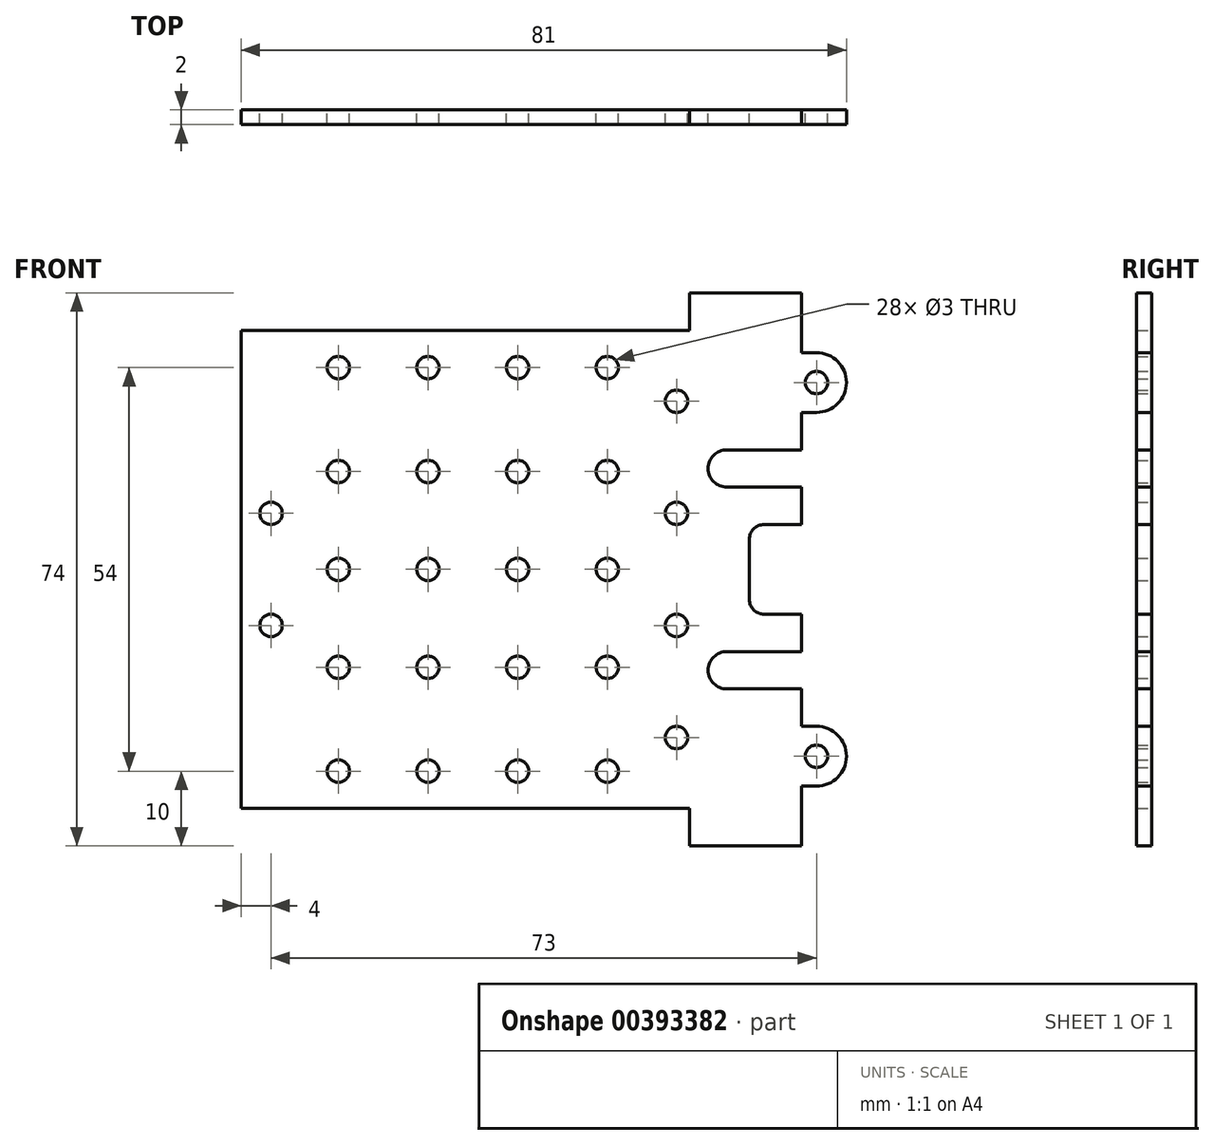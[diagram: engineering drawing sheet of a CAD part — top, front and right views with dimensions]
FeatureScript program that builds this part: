
annotation { "Feature Type Name" : "Feature", "Feature Type Description" : "" }
export const myFeature = defineFeature(function(context is Context, id is Id, definition is map)
    precondition{}
    {
        {
            var Q0;
            Q0=qCreatedBy(makeId("Front.planeOp"),FACE);
            var sketch = newSketch(context, id + "F0", { "sketchPlane" : qUnion([Q0])});
            skLineSegment(sketch, "E0.bottom", {"start": v(-37.5, 16) * mm, "end": v(22.5, 16) * mm});
            skLineSegment(sketch, "E0.right", {"start": v(37.5, 16) * mm, "end": v(37.5, 13) * mm});
            skLineSegment(sketch, "E1", {"start": v(37.5, 16) * mm, "end": v(37.5, 21) * mm});
            skLineSegment(sketch, "E2", {"start": v(37.5, 21) * mm, "end": v(22.5, 21) * mm});
            skLineSegment(sketch, "E3", {"start": v(22.5, 21) * mm, "end": v(22.5, 16) * mm});
            skLineSegment(sketch, "E4", {"start": v(37.5, 13) * mm, "end": v(39.5, 13) * mm});
            skLineSegment(sketch, "E5", {"start": v(39.5, 5) * mm, "end": v(37.5, 5) * mm});
            skArc(sketch, "E6", {"start": v(39.5, 13) * mm, "mid": v(43.5, 9) * mm, "end": v(39.5, 5) * mm});
            skLineSegment(sketch, "E7", {"start": v(37.5, 0) * mm, "end": v(27.5, 0) * mm});
            skLineSegment(sketch, "E8", {"start": v(27.5, -5) * mm, "end": v(37.5, -5) * mm});
            skLineSegment(sketch, "E9", {"start": v(37.5, -10) * mm, "end": v(30.5, -10) * mm});
            skLineSegment(sketch, "E10", {"start": v(30.5, -10) * mm, "end": v(30.5, -16) * mm});
            skArc(sketch, "E11", {"start": v(27.5, 0) * mm, "mid": v(25, -2.5) * mm, "end": v(27.5, -5) * mm});
            skLineSegment(sketch, "E12.trimOffspring", {"start": v(37.5, -5) * mm, "end": v(37.5, -10) * mm});
            skPoint(sketch, "E13.orphan", {"position": v(37.5, -16) * mm});
            skLineSegment(sketch, "E14.trimOffspring", {"start": v(37.5, 5) * mm, "end": v(37.5, 0) * mm});
            skCircle(sketch, "E15", {"center": v(-24.5, 11) * mm, "radius": 1.5 * mm});
            skCircle(sketch, "E16.0.1.0", {"center": v(-24.5, -2.9) * mm, "radius": 1.5 * mm});
            skCircle(sketch, "E16.1.0.0", {"center": v(-12.5, 11) * mm, "radius": 1.5 * mm});
            skCircle(sketch, "E16.1.1.0", {"center": v(-12.5, -2.9) * mm, "radius": 1.5 * mm});
            skCircle(sketch, "E16.2.0.0", {"center": v(-0.5, 11) * mm, "radius": 1.5 * mm});
            skCircle(sketch, "E16.2.1.0", {"center": v(-0.5, -2.9) * mm, "radius": 1.5 * mm});
            skCircle(sketch, "E16.3.0.0", {"center": v(11.5, 11) * mm, "radius": 1.5 * mm});
            skCircle(sketch, "E16.3.1.0", {"center": v(11.5, -2.9) * mm, "radius": 1.5 * mm});
            skLineSegment(sketch, "E16.direction1", {"start": v(-24.5, 11) * mm, "end": v(-12.5, 11) * mm, "construction": true});
            skLineSegment(sketch, "E16.direction2", {"start": v(-24.5, 11) * mm, "end": v(-24.5, -2.9) * mm, "construction": true});
            skLineSegment(sketch, "E17", {"start": v(-37.5, 16) * mm, "end": v(-37.5, -16) * mm});
            skLineSegment(sketch, "E18", {"start": v(-37.5, -16) * mm, "end": v(30.5, -16) * mm});
            skArc(sketch, "E19", {"start": v(-26, -16) * mm, "mid": v(-24.5, -14.5) * mm, "end": v(-23, -16) * mm});
            skArc(sketch, "E20.1.0.0", {"start": v(-14, -16) * mm, "mid": v(-12.5, -14.5) * mm, "end": v(-11, -16) * mm});
            skArc(sketch, "E20.2.0.0", {"start": v(-2, -16) * mm, "mid": v(-0.5, -14.5) * mm, "end": v(1, -16) * mm});
            skArc(sketch, "E20.3.0.0", {"start": v(10, -16) * mm, "mid": v(11.5, -14.5) * mm, "end": v(13, -16) * mm});
            skLineSegment(sketch, "E20.direction1", {"start": v(-26, -16) * mm, "end": v(-14, -16) * mm, "construction": true});
            skCircle(sketch, "E21", {"center": v(-33.5, -8.5) * mm, "radius": 1.5 * mm});
            skCircle(sketch, "E22", {"center": v(20.76, -8.5) * mm, "radius": 1.5 * mm});
            skCircle(sketch, "E23.0.1.0", {"center": v(20.76, 6.5) * mm, "radius": 1.5 * mm});
            skLineSegment(sketch, "E23.direction2", {"start": v(20.76, -8.5) * mm, "end": v(20.76, 6.5) * mm, "construction": true});
            skCircle(sketch, "E24", {"center": v(39.5, 9) * mm, "radius": 1.5 * mm});
            skArc(sketch, "E25.MirrorCS", {"start": v(-14, -16) * mm, "mid": v(-12.5, -17.5) * mm, "end": v(-11, -16) * mm});
            skLineSegment(sketch, "E26.MirrorCS", {"start": v(39.5, -37) * mm, "end": v(37.5, -37) * mm});
            skLineSegment(sketch, "E27.MirrorCS", {"start": v(37.5, -48) * mm, "end": v(37.5, -45) * mm});
            skLineSegment(sketch, "E28.MirrorCS", {"start": v(37.5, -45) * mm, "end": v(39.5, -45) * mm});
            skCircle(sketch, "E29.MirrorC", {"center": v(-24.5, -29.1) * mm, "radius": 1.5 * mm});
            skArc(sketch, "E30.MirrorCS", {"start": v(-26, -16) * mm, "mid": v(-24.5, -17.5) * mm, "end": v(-23, -16) * mm});
            skArc(sketch, "E31.MirrorCS", {"start": v(10, -16) * mm, "mid": v(11.5, -17.5) * mm, "end": v(13, -16) * mm});
            skArc(sketch, "E32.MirrorCS", {"start": v(-2, -16) * mm, "mid": v(-0.5, -17.5) * mm, "end": v(1, -16) * mm});
            skCircle(sketch, "E33.MirrorC", {"center": v(-0.5, -29.1) * mm, "radius": 1.5 * mm});
            skLineSegment(sketch, "E34.MirrorCS", {"start": v(37.5, -22) * mm, "end": v(30.5, -22) * mm});
            skCircle(sketch, "E35.MirrorC", {"center": v(20.76, -38.5) * mm, "radius": 1.5 * mm});
            skArc(sketch, "E36.MirrorCS", {"start": v(39.5, -45) * mm, "mid": v(43.5, -41) * mm, "end": v(39.5, -37) * mm});
            skLineSegment(sketch, "E37.MirrorCS", {"start": v(-24.5, -43) * mm, "end": v(-12.5, -43) * mm, "construction": true});
            skCircle(sketch, "E38.MirrorC", {"center": v(-33.5, -23.5) * mm, "radius": 1.5 * mm});
            skCircle(sketch, "E39.MirrorC", {"center": v(-12.5, -29.1) * mm, "radius": 1.5 * mm});
            skLineSegment(sketch, "E40.MirrorCS", {"start": v(37.5, -48) * mm, "end": v(37.5, -53) * mm});
            skLineSegment(sketch, "E41.MirrorCS", {"start": v(-24.5, -43) * mm, "end": v(-24.5, -29.1) * mm, "construction": true});
            skLineSegment(sketch, "E42.MirrorCS", {"start": v(20.76, -23.5) * mm, "end": v(20.76, -38.5) * mm, "construction": true});
            skLineSegment(sketch, "E43.MirrorCS", {"start": v(30.5, -22) * mm, "end": v(30.5, -16) * mm});
            skArc(sketch, "E44.MirrorCS", {"start": v(27.5, -32) * mm, "mid": v(25, -29.5) * mm, "end": v(27.5, -27) * mm});
            skLineSegment(sketch, "E45.MirrorCS", {"start": v(27.5, -27) * mm, "end": v(37.5, -27) * mm});
            skLineSegment(sketch, "E46.MirrorCS", {"start": v(-37.5, -48) * mm, "end": v(22.5, -48) * mm});
            skLineSegment(sketch, "E47.MirrorCS", {"start": v(22.5, -53) * mm, "end": v(22.5, -48) * mm});
            skCircle(sketch, "E48.MirrorC", {"center": v(11.5, -43) * mm, "radius": 1.5 * mm});
            skLineSegment(sketch, "E49.MirrorCS", {"start": v(37.5, -37) * mm, "end": v(37.5, -32) * mm});
            skLineSegment(sketch, "E50.MirrorCS", {"start": v(-37.5, -48) * mm, "end": v(-37.5, -16) * mm});
            skCircle(sketch, "E51.MirrorC", {"center": v(-12.5, -43) * mm, "radius": 1.5 * mm});
            skLineSegment(sketch, "E52.MirrorCS", {"start": v(37.5, -32) * mm, "end": v(27.5, -32) * mm});
            skCircle(sketch, "E53.MirrorC", {"center": v(-24.5, -43) * mm, "radius": 1.5 * mm});
            skCircle(sketch, "E54.MirrorC", {"center": v(11.5, -29.1) * mm, "radius": 1.5 * mm});
            skLineSegment(sketch, "E55.MirrorCS", {"start": v(37.5, -27) * mm, "end": v(37.5, -22) * mm});
            skLineSegment(sketch, "E56.MirrorCS", {"start": v(37.5, -53) * mm, "end": v(22.5, -53) * mm});
            skCircle(sketch, "E57.MirrorC", {"center": v(39.5, -41) * mm, "radius": 1.5 * mm});
            skCircle(sketch, "E58.MirrorC", {"center": v(-0.5, -43) * mm, "radius": 1.5 * mm});
            skCircle(sketch, "E59.MirrorC", {"center": v(20.76, -23.5) * mm, "radius": 1.5 * mm});
            skSolve(sketch);
        }
        {
            var Q0;
            Q0=makeQuery(id+"F0.imprint","IMPRINT",FACE,{"disambiguationData":[TD([[makeQuery(id+"F0.imprint","IMPRINT",EDGE,{"derivedFrom":sQuery(id+"F0.wireOp",EDGE,"E0.bottom")}),-1.0]])]});
            var Q1;
            {var subQ7=sQuery(id+"F0.wireOp",EDGE,"E25.MirrorCS");Q1=makeQuery(id+"F0.imprint","IMPRINT",FACE,{"disambiguationData":[TD([[makeQuery(id+"F0.imprint","IMPRINT",EDGE,{"derivedFrom":subQ7}),-1.0]])]});}
            extrude(context, id + "F1", {"entities" : qUnion([Q0, Q1]), "depth" : 2 * mm});
        }
        {
            var Q0;
            Q0=makeQuery(id+"F1.opExtrude","SWEPT_EDGE",EDGE,{"disambiguationData":[OSD([sQuery(id+"F0.wireOp",EDGE,"E34.MirrorCS"),sQuery(id+"F0.wireOp",EDGE,"E43.MirrorCS")])]});
            var Q1;
            Q1=makeQuery(id+"F1.opExtrude","SWEPT_EDGE",EDGE,{"disambiguationData":[OSD([sQuery(id+"F0.wireOp",EDGE,"E9"),sQuery(id+"F0.wireOp",EDGE,"E10")])]});
            fillet(context, id + "F2", {"entities" : qUnion([Q0, Q1]), "radius" : 2 * mm, "tangentPropagation" : true, "allowEdgeOverflow" : false});
        }
    });
